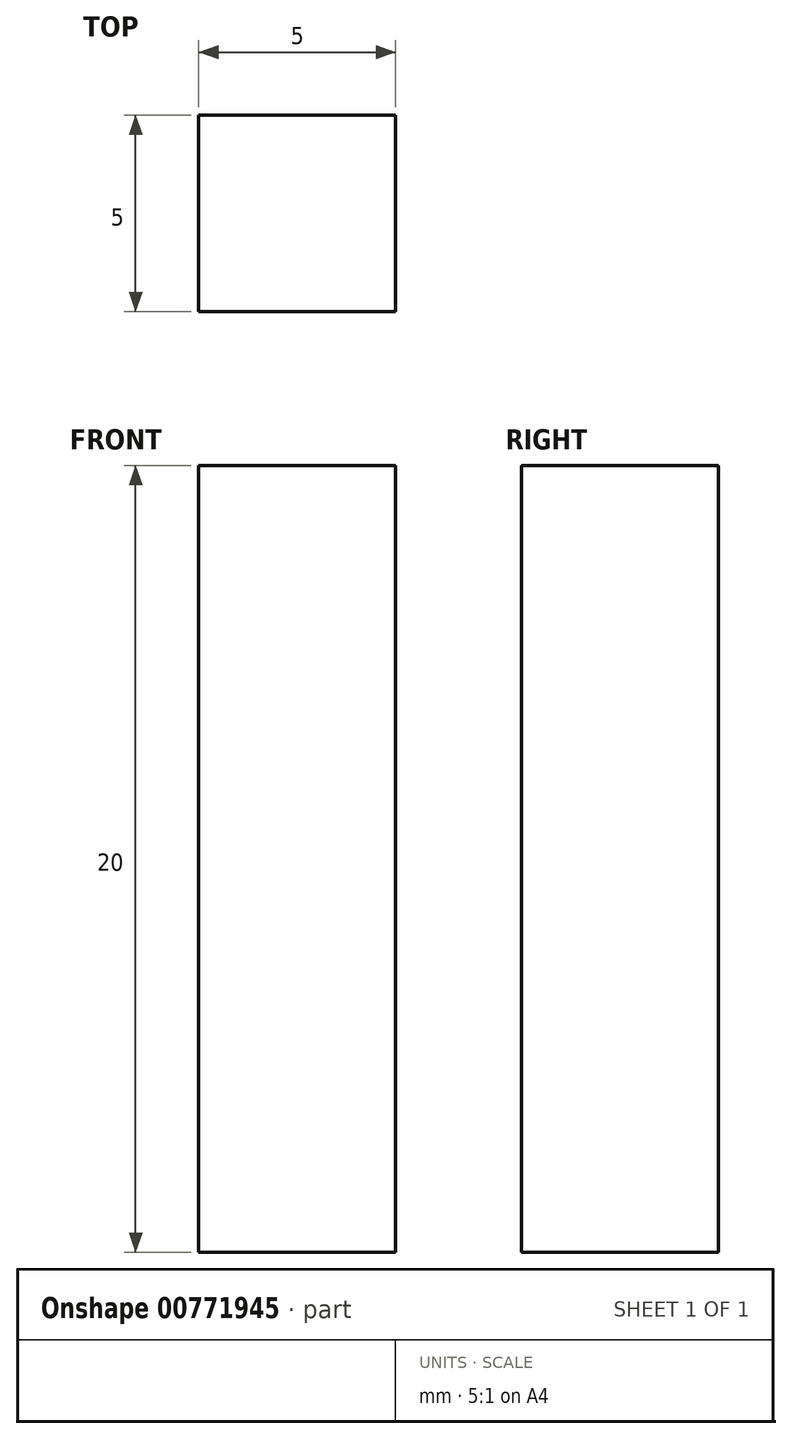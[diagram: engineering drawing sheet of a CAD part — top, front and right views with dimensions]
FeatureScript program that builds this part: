
annotation { "Feature Type Name" : "Feature", "Feature Type Description" : "" }
export const myFeature = defineFeature(function(context is Context, id is Id, definition is map)
    precondition{}
    {
        {
            var Q0;
            Q0=qCreatedBy(makeId("Top.planeOp"),FACE);
            var sketch = newSketch(context, id + "F0", { "sketchPlane" : qUnion([Q0])});
            skLineSegment(sketch, "E0.bottom", {"start": v(0, 0) * mm, "end": v(5, 0) * mm});
            skLineSegment(sketch, "E0.top", {"start": v(0, 5) * mm, "end": v(5, 5) * mm});
            skLineSegment(sketch, "E0.left", {"start": v(0, 0) * mm, "end": v(0, 5) * mm});
            skLineSegment(sketch, "E0.right", {"start": v(5, 0) * mm, "end": v(5, 5) * mm});
            skSolve(sketch);
        }
        {
            var Q0;
            Q0=makeQuery(id+"F0.imprint","IMPRINT",FACE,{"disambiguationData":[TD([[makeQuery(id+"F0.imprint","IMPRINT",EDGE,{"derivedFrom":sQuery(id+"F0.wireOp",EDGE,"E0.bottom")}),1.0]])]});
            extrude(context, id + "F1", {"entities" : qUnion([Q0]), "depth" : 20 * mm, "offsetDistance" : 25 * mm});
        }
    });
